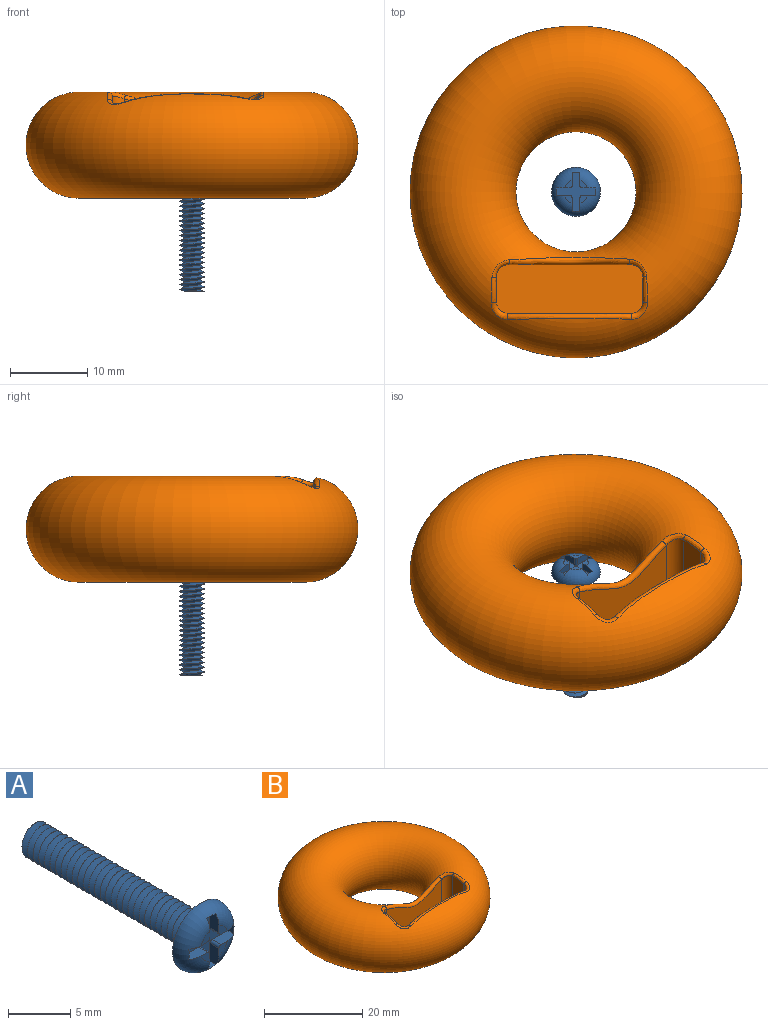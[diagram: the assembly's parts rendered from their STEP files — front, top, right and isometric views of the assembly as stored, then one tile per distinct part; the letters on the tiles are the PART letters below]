
ASSEMBLY  parts=2 mates=1
PART A: 28 faces, bbox 6.9x21.6x6.9 mm
  f0: cylinder r=1.59mm len=19.05mm, axis (0,-1,0), area -64.5mm2, adj f5,f24,f25,f26,f27
  f1: plane 0.98x0.98mm, normal (0,-1,0), area 0.6mm2, adj f4,f9,f10,f20
  f2: plane 0.98x0.98mm, normal (0,-1,0), area 0.6mm2, adj f4,f12,f13,f21
  f3: plane 0.98x0.98mm, normal (0,-1,0), area 0.6mm2, adj f4,f15,f16,f22
  f4: torus R=1.57mm, axis (0,1,0), area 36.1mm2, adj f1,f2,f3,f5,f6,f7,f8,f9
  f5: plane 6.35x6.35mm, normal (0,1,0), area 23.8mm2, adj f0,f4
  f6: plane 0.98x0.98mm, normal (0,-1,0), area 0.6mm2, adj f4,f7,f18,f19
  f7: plane 1.86x1.1mm, normal (0,0,-1), area 1.7mm2, adj f4,f6,f8,f19,f23
  f8: plane 1.02x0.69mm, normal (1,0,0), area 0.7mm2, adj f4,f7,f9,f23
  f9: plane 1.86x1.1mm, normal (0,0,1), area 1.7mm2, adj f1,f4,f8,f20,f23
  f10: plane 1.86x1.1mm, normal (1,0,0), area 1.7mm2, adj f1,f4,f11,f20,f23
  f11: plane 1.02x0.69mm, normal (0,0,1), area 0.7mm2, adj f4,f10,f12,f23
  f12: plane 1.86x1.1mm, normal (-1,0,0), area 1.7mm2, adj f2,f4,f11,f21,f23
  f13: plane 1.86x1.1mm, normal (0,0,1), area 1.7mm2, adj f2,f4,f14,f21,f23
  f14: plane 1.02x0.69mm, normal (-1,0,0), area 0.7mm2, adj f4,f13,f15,f23
  f15: plane 1.86x1.1mm, normal (0,0,-1), area 1.7mm2, adj f3,f4,f14,f22,f23
  f16: plane 1.86x1.1mm, normal (-1,0,0), area 1.7mm2, adj f3,f4,f17,f22,f23
  f17: plane 1.02x0.69mm, normal (0,0,-1), area 0.7mm2, adj f4,f16,f18,f23
  f18: plane 1.86x1.1mm, normal (1,0,0), area 1.7mm2, adj f4,f6,f17,f19,f23
  f19: cylinder r=0.25mm len=1.02mm, axis (0,-1,0), area 0.4mm2, adj f6,f7,f18,f23
  f20: cylinder r=0.25mm len=1.02mm, axis (0,-1,0), area 0.4mm2, adj f1,f9,f10,f23
  f21: cylinder r=0.25mm len=1.02mm, axis (0,-1,0), area 0.4mm2, adj f2,f12,f13,f23
  f22: cylinder r=0.25mm len=1.02mm, axis (0,-1,0), area 0.4mm2, adj f3,f15,f16,f23
  f23: plane 5.08x5.08mm, normal (0,-1,0), area 9.3mm2, adj f7,f8,f9,f10,f11,f12,f13,f14
  f24: plane 3.11x3.11mm, normal (0,1,0), area 5.2mm2, adj f0,f26,f27
  f25: plane 0.64x0.62mm, normal (0,0,-1), area 0.2mm2, adj f0,f26,f27
  f26: bspline ~19.35x3.67mm, area 167.1mm2, adj f0,f24,f25,f27
  f27: bspline ~19.16x3.67mm, area 166mm2, adj f0,f24,f25,f26
PART B: 18 faces, bbox 46.7x46.7x13.8 mm
  f0: torus R=14.67mm, axis (0,0,-1), area 3815.6mm2, adj f10,f11,f12,f13,f14,f15,f16,f17
  f1: plane 10.06x3.18mm, normal (1,0,0), area 30.9mm2, adj f5,f6,f9,f11
  f2: plane 15.88x9.9mm, normal (0,1,0), area 153.3mm2, adj f5,f6,f7,f12
  f3: plane 10.11x3.18mm, normal (-1,0,0), area 31.7mm2, adj f5,f7,f8,f16
  f4: plane 15.88x9.74mm, normal (0,-1,0), area 125.2mm2, adj f5,f8,f9,f15
  f5: plane 19.05x6.35mm, normal (0,0,1), area 118.8mm2, adj f1,f2,f3,f4,f6,f7,f8,f9
  f6: cylinder r=1.59mm len=9.24mm, axis (0,0,-1), area 21.9mm2, adj f1,f2,f5,f10
  f7: cylinder r=1.59mm len=9.7mm, axis (0,0,1), area 23.3mm2, adj f2,f3,f5,f14
  f8: cylinder r=1.59mm len=10.11mm, axis (0,0,-1), area 24.4mm2, adj f3,f4,f5,f17
  f9: cylinder r=1.59mm len=10.11mm, axis (0,0,1), area 25mm2, adj f1,f4,f5,f13
  f10: bspline ~2.75x2.63mm, area 3.1mm2, adj f0,f6,f11,f12
  f11: bspline ~7.11x2.2mm, area 3.1mm2, adj f0,f1,f10,f13
  f12: bspline ~18.03x2.15mm, area 15.8mm2, adj f0,f2,f10,f14
  f13: bspline ~2.76x2.72mm, area 2.4mm2, adj f0,f9,f11,f15
  f14: bspline ~2.68x2.59mm, area 2.9mm2, adj f0,f7,f12,f16
  f15: bspline ~18.38x4.11mm, area 19.8mm2, adj f0,f4,f13,f17
  f16: bspline ~8.08x1.57mm, area 2.8mm2, adj f0,f3,f14,f17
  f17: bspline ~2.77x2.65mm, area 2.6mm2, adj f0,f8,f15,f16
PLACE A rot(axis=(-1,0,0),90deg) t=(-58.11,-6.55,35.24)mm
PLACE B t=(-58.11,-6.55,31.5)mm
MATE fastened A.f0 <-> B.f0  axis (0,0,-1) through (-58.11,-6.55,35.24)mm
